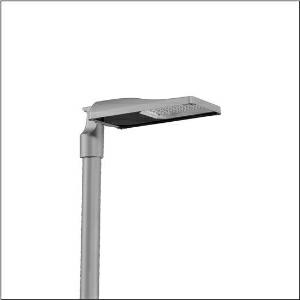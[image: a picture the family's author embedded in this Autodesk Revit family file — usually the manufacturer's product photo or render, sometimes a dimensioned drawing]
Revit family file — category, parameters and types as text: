
# Revit family: streetlight_sl_31_mini___st1_0a_5xh2d31a08ga_4fc3
name_source: partatom
category: Lighting Fixtures
units: mm (PartAtom-declared; Revit-internal decimal feet)

## family parameters
Cut with Voids When Loaded = No
Host = Face
Light Source = No
Part Type = Normal
Room Calculation Point = No
Round Connector Dimension = Use Diameter
Shared = No

## types (1)
- --- (1 x LED, 5710 lm, 37.3 W, 3000K)
    Apparent Load = 37 VA
    CIE Flux Codes = 37 72 97 100 100
    Color Rendering = 70
    Color Temperature = 3000K
    Default Elevation = 1800 mm
    Description = Streetlight SL 31 mini Easy, Desk-Remote mast luminaire for post-top, side-entry; light control with lens of PMMA; light distribution: ST1.0a, direct asymmetric distribution, for standard-compliant lighting for roads and squares; LED: luminous flux: 5.710lm, light colour: 730, colour temperature: 3000K; luminous efficacy: 153,1lm/W; control: pre-setting: linear dimming characteristic, flexible luminous flux parameterisation, time-dependent luminous flux control, constant luminous flux control, intelligent temperature release in ECG and LED module, overheat protection; luminaire housing, of diecast aluminium, Siteco® metallic grey (DB 702S), corrosivity category C5 high according to DIN EN ISO 12944; cover of toughened safety glass, transparent, mast flange of diecast aluminium, Siteco® metallic grey (DB 702S), spigot size: 76/60mm, mast flange included unmounted; with cable H07RN-F 2x 1.5mm², cable length: 6,5m, connection cable pre-assembled; mains connection: 220..240V, AC, 50/60Hz; power consumption (at start of service life): 37,3W / (at end of service life): 38,7W / (with reduced operation 50%): 17,5W; protection rating (complete): IP66; insulation class (complete): insulation class II (safety insulation); impact resistance: IK10; certification: CE, ENEC, ENEC+, VDE, UKCA; permissible operating ambient temperature for outdoor applications: -40..+50°C; packaging unit: 1 piece

Light Distribution: ST1.0a
    Height = 76 mm
    Lamp = 1 x LED
    Lamp Light Flux = 5710 lm
    Lamp Power = 37.3 W
    Lamp count = 1
    Length = 547 mm
    Luminous efficacy = 153 lm/W
    Manufacturer = Siteco
    ModVariant = No
    Model = 5XH2D31A08GA
    Number of Poles = 1
    OnlyDefault = Yes
    Power Factor = 1
    Product Name = Streetlight SL 31 mini | ST1.0a
    Product group = mast luminaire | pylon top
    ProductGroupID = 6100
    Protection Class = Protection class II
    Protection Degree = IP 66
    RLX_Detail_Level = 1
    RLX_Emergency_Light_Flux = 0 lm
    RLX_Emergency_Type = 0
    RLX_Emergency_Type_DB = No
    RlxData = <blob elided: 39521 chars, md5=a2f21d2c>
    Socket = socket
    Standby Power = 0 W
    System Light Flux = 5710 lm
    System Power = 37 W
    Type Comments = factory setting: luminous flux: 100 % | dim-lin: 254 | 386 mA
    Type Image = l_1300326.jpg
    URL = http://relux.com
    VarID = @adj_075567
    Voltage = 0 V
    Weight = 0.00 kg
    Width = 265 mm

## geometry (parser evidence)
native form markers: Blend x4, Sweep x9
no freeform markers — native parametric forms only
